# Revit family: xBall_Valve-McGuire-Convertible_II-LFBV2-4PST53
name_source: partatom
category: Plumbing Fixtures
revit_build: Autodesk Revit 2014 (Build: 20130308_1515(x64)
units: mm (PartAtom-declared; Revit-internal decimal feet)

## types (1)
- LFBV2-4PST53
    A Length = 1 1/2"
    Assembly Code = D2020300
    B Length = 2 3/16"
    CW Connection = Yes
    CWFU = 0
    Default Elevation = 0"
    Description = McGuire's convertible quarter-turn brass ball valve. Straight Stop, 1/2” CPVC x 3/8” OD. All components are chrome plated.
    Finish = Brass-McGuire-Chrome Plated
    HW Connection = Yes
    HWFU = 0
    Hydronic Supply Diameter = 1/2"
    Hydronic Supply Radius = 1/4"
    IAPMO Compliance = cUPC Lead Free
    Manufacturer = McGuire Mfg
    Material = Brass-McGuire-Chrome Plated
    Model = LFBV2-4PST53
    Outlet Diameter = 3/8"
    Outlet Radius = 3/16"
    Price = Prices may vary. Please consult Manufacturer Representative for most up-to-date price list.
    Product Documentation Link = http://products.mcguiremfg.com
    Product Page URL = http://products.mcguiremfg.com
    Revised Date = 01/10/2018
    Shipping Weight = 0.41 lb
    Specification = Lead free convertible quarter-turn brass ball valve, chrome plated commercial valve with convertible loose key handle. Supply stop valve shall be certified by recognized testing authority and bear manufacturer and testing mark.
    URL = http://www.mcguiremfg.com
    Vent Connection = No
    WFU = 0
    Warranty Information = 3 Years Limited Warranty
    Waste Connection = No

## geometry (parser evidence)
native form markers: Sweep x1
no freeform markers — native parametric forms only
